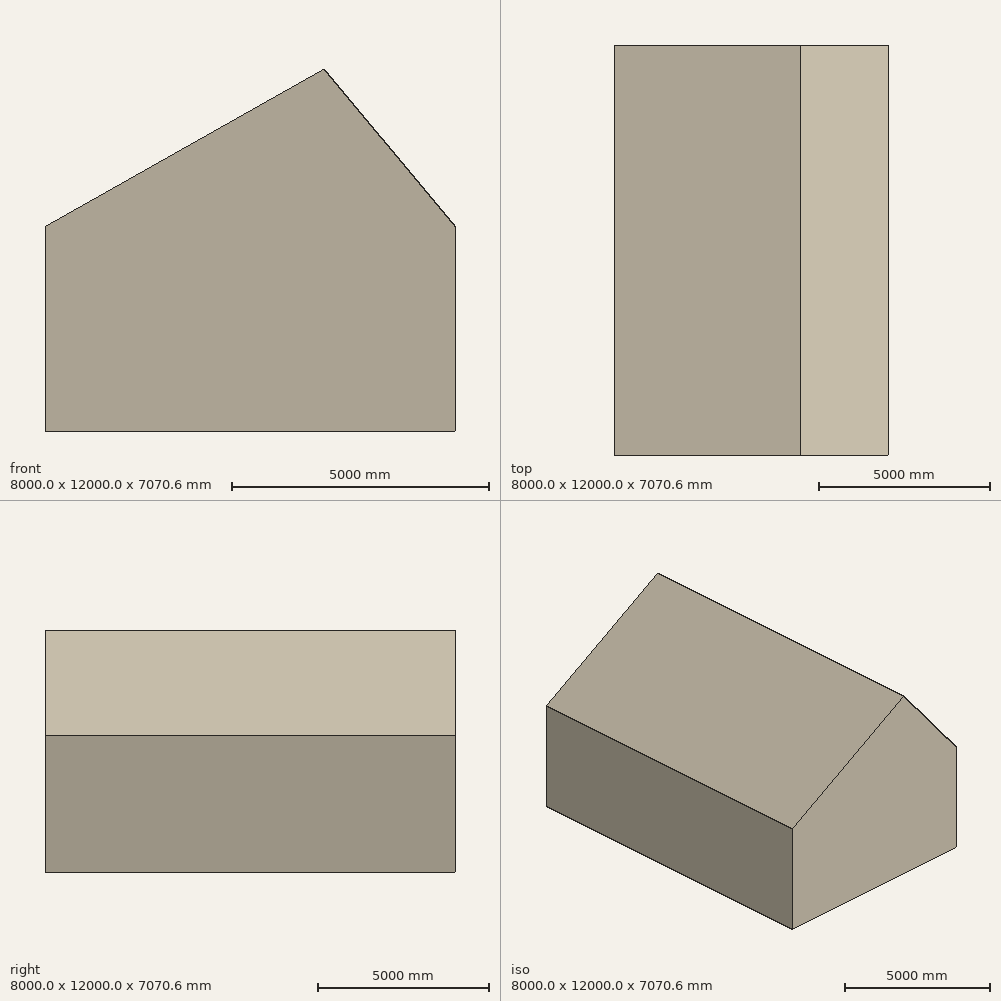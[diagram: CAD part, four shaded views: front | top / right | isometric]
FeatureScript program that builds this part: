
annotation { "Feature Type Name" : "Feature", "Feature Type Description" : "" }
export const myFeature = defineFeature(function(context is Context, id is Id, definition is map)
    precondition{}
    {
        {
            var Q0;
            Q0=qCreatedBy(makeId("Front.planeOp"),FACE);
            var sketch = newSketch(context, id + "F0", { "sketchPlane" : qUnion([Q0])});
            skLineSegment(sketch, "E0", {"start": v(0, 0) * mm, "end": v(5436.54, 3070.62) * mm});
            skLineSegment(sketch, "E1", {"start": v(5436.54, 3070.62) * mm, "end": v(8000, 0) * mm});
            skLineSegment(sketch, "E2", {"start": v(8000, 0) * mm, "end": v(8000, -4000) * mm});
            skLineSegment(sketch, "E3", {"start": v(8000, -4000) * mm, "end": v(0, -4000) * mm});
            skLineSegment(sketch, "E4", {"start": v(0, -4000) * mm, "end": v(0, 0) * mm});
            skSolve(sketch);
        }
        {
            var Q0;
            Q0=makeQuery(id+"F0.imprint","IMPRINT",FACE,{"disambiguationData":[TD([[makeQuery(id+"F0.imprint","IMPRINT",EDGE,{"derivedFrom":sQuery(id+"F0.wireOp",EDGE,"E0")}),-1.0]])]});
            extrude(context, id + "F1", {"entities" : qUnion([Q0]), "depth" : 12000 * mm});
        }
    });
